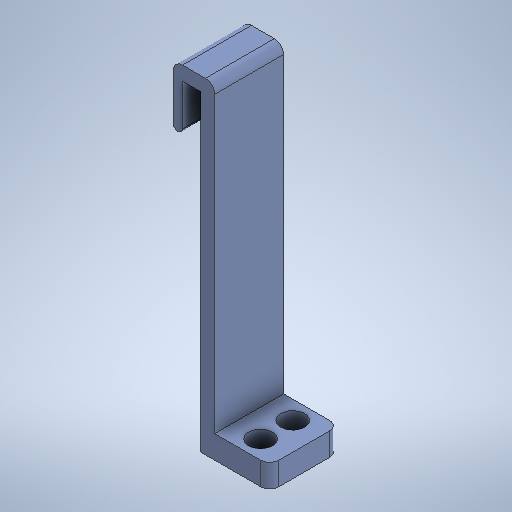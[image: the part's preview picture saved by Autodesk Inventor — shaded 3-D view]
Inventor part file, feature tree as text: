
AUTODESK INVENTOR PART (.ipt)
format: ipt  version: 2025 (Build 290162000, 162)  size: 451,584 bytes
history: native  units: mm
features: fillet x3, extrude x2, sketch x2
ambient origin geometry x8: Origin, YZ Plane, XZ Plane, XY Plane, X Axis, Y Axis, Z Axis, Center Point
bodies: Solide1 (feature_tree)
feature tree (7):
  extrude  "Extrusion1"  Depth=15.0mm TaperAngle=0.0deg
  extrude  "Extrusion2"  Depth=5.2mm
  fillet  "Congé2"  Radius=5.2mm
  fillet  "Congé3"  Radius=4.0mm
  fillet  "Congé4"  Radius=4.0mm
  sketch  "Esquisse1"
  sketch  "Esquisse2"
